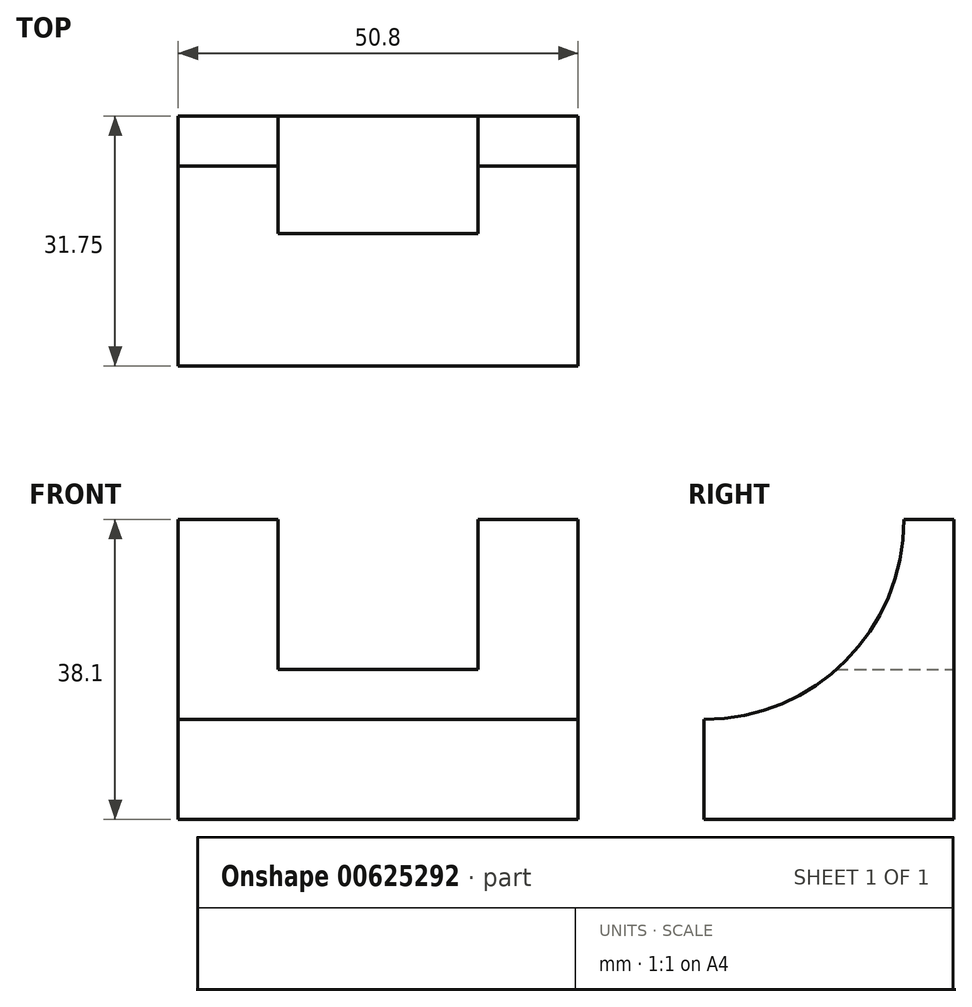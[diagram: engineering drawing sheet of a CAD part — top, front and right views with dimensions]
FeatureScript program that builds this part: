
annotation { "Feature Type Name" : "Feature", "Feature Type Description" : "" }
export const myFeature = defineFeature(function(context is Context, id is Id, definition is map)
    precondition{}
    {
        {
            var Q0;
            Q0=qCreatedBy(makeId("Right.planeOp"),FACE);
            var sketch = newSketch(context, id + "F0", { "sketchPlane" : qUnion([Q0])});
            skLineSegment(sketch, "E0", {"start": v(0, 0) * mm, "end": v(-31.75, 0) * mm});
            skLineSegment(sketch, "E1", {"start": v(-31.75, 0) * mm, "end": v(-31.75, 12.7) * mm});
            skLineSegment(sketch, "E2", {"start": v(0, 0) * mm, "end": v(0, 38.1) * mm});
            skLineSegment(sketch, "E3", {"start": v(0, 38.1) * mm, "end": v(-6.35, 38.1) * mm});
            skArc(sketch, "E4", {"start": v(-31.75, 12.7) * mm, "mid": v(-13.79, 20.14) * mm, "end": v(-6.35, 38.1) * mm});
            skSolve(sketch);
        }
        {
            var Q0;
            Q0 = qSketchRegion(id + "F0", true);
            extrude(context, id + "F1", {"entities" : qUnion([Q0]), "depth" : 50.8 * mm, "offsetDistance" : 25.4 * mm});
        }
        {
            var Q0;
            Q0=makeQuery(id+"F1.opExtrude","SWEPT_FACE",FACE,{"disambiguationData":[OSD([sQuery(id+"F0.wireOp",EDGE,"E2")])]});
            var sketch = newSketch(context, id + "F2", { "sketchPlane" : qUnion([Q0])});
            skLineSegment(sketch, "E5", {"start": v(-38.1, 38.1) * mm, "end": v(-38.1, 19.05) * mm});
            skLineSegment(sketch, "E6", {"start": v(-38.1, 19.05) * mm, "end": v(-12.7, 19.05) * mm});
            skLineSegment(sketch, "E7", {"start": v(-12.7, 19.05) * mm, "end": v(-12.7, 38.1) * mm});
            skSolve(sketch);
        }
        {
            var Q0;
            {var subQ0=sQuery(id+"F2.wireOp",EDGE,"E5");Q0=makeQuery(id+"F2.imprint","IMPRINT",FACE,{"disambiguationData":[TD([[makeQuery(id+"F2.imprint","IMPRINT",EDGE,{"derivedFrom":subQ0}),1.0]])]});}
            extrude(context, id + "F3", {"entities" : qUnion([Q0]), "operationType" : NewBodyOperationType.REMOVE, "oppositeDirection" : true, "depth" : 25.4 * mm, "offsetDistance" : 25.4 * mm});
        }
    });
